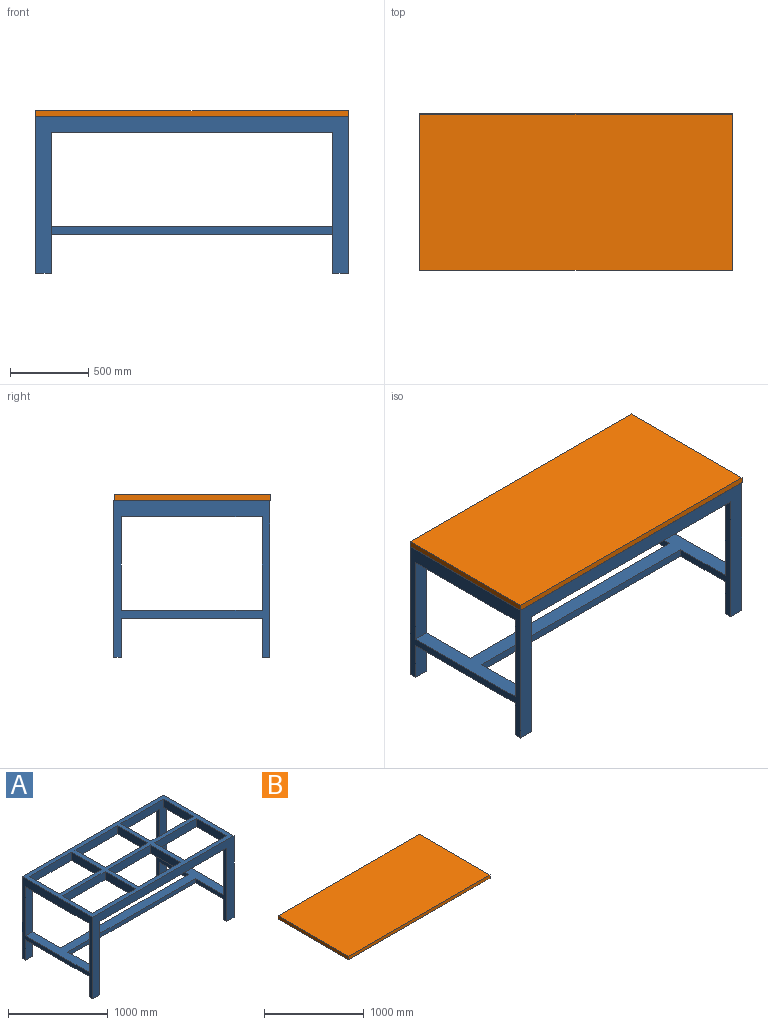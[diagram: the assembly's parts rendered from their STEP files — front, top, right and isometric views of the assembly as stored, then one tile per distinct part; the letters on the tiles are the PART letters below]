
ASSEMBLY  parts=2 mates=1
PART A: 46 faces, bbox 2000x1000x1000 mm
  f0: plane 900x450mm, normal (-1,0,0), area 65000mm2, adj f3,f6,f11,f31,f37,f42,f43,f44
  f1: plane 900x450mm, normal (1,0,0), area 65000mm2, adj f4,f6,f11,f15,f40,f42,f43,f44
  f2: plane 700x650mm, normal (0,1,0), area 120000mm2, adj f6,f7,f10,f16,f18,f36,f43
  f3: plane 700x650mm, normal (0,-1,0), area 120000mm2, adj f0,f6,f7,f10,f28,f30,f43
  f4: plane 700x650mm, normal (0,-1,0), area 120000mm2, adj f1,f6,f7,f8,f12,f14,f43
  f5: plane 700x650mm, normal (0,1,0), area 120000mm2, adj f6,f7,f8,f20,f22,f38,f43
  f6: plane 2000x1000mm, normal (0,0,-1), area 450000mm2, adj f0,f1,f2,f3,f4,f5,f8,f9
  f7: plane 2000x1000mm, normal (0,0,1), area 470000mm2, adj f2,f3,f4,f5,f8,f9,f10,f11
  f8: plane 1000x1000mm, normal (-1,0,0), area 235000mm2, adj f4,f5,f6,f7,f9,f11,f15,f21
  f9: plane 2000x1000mm, normal (0,-1,0), area 380000mm2, adj f6,f7,f8,f10,f36,f38,f39,f41
  f10: plane 1000x1000mm, normal (1,0,0), area 235000mm2, adj f2,f3,f6,f7,f9,f11,f17,f31
  f11: plane 2000x1000mm, normal (0,1,0), area 380000mm2, adj f0,f1,f6,f7,f8,f10,f37,f40
  f12: plane 425x100mm, normal (1,0,0), area 42500mm2, adj f4,f6,f7,f13
  f13: plane 600x100mm, normal (0,1,0), area 60000mm2, adj f6,f7,f12,f14
  f14: plane 425x100mm, normal (-1,0,0), area 42500mm2, adj f4,f6,f7,f13
  f15: plane 250x100mm, normal (0,-1,0), area 25000mm2, adj f1,f8,f40,f42
  f16: plane 425x100mm, normal (1,0,0), area 42500mm2, adj f2,f6,f7,f19
  f17: plane 250x100mm, normal (0,1,0), area 25000mm2, adj f10,f36,f41,f42
  f18: plane 425x100mm, normal (-1,0,0), area 42500mm2, adj f2,f6,f7,f19
  f19: plane 600x100mm, normal (0,-1,0), area 60000mm2, adj f6,f7,f16,f18
  f20: plane 425x100mm, normal (1,0,0), area 42500mm2, adj f5,f6,f7,f23
  f21: plane 250x100mm, normal (0,1,0), area 25000mm2, adj f8,f38,f39,f42
  f22: plane 425x100mm, normal (-1,0,0), area 42500mm2, adj f5,f6,f7,f23
  f23: plane 600x100mm, normal (0,-1,0), area 60000mm2, adj f6,f7,f20,f22
  f24: plane 425x100mm, normal (1,0,0), area 42500mm2, adj f6,f7,f25,f27
  f25: plane 600x100mm, normal (0,1,0), area 60000mm2, adj f6,f7,f24,f26
  f26: plane 425x100mm, normal (-1,0,0), area 42500mm2, adj f6,f7,f25,f27
  f27: plane 600x100mm, normal (0,-1,0), area 60000mm2, adj f6,f7,f24,f26
  f28: plane 425x100mm, normal (1,0,0), area 42500mm2, adj f3,f6,f7,f29
  f29: plane 600x100mm, normal (0,1,0), area 60000mm2, adj f6,f7,f28,f30
  f30: plane 425x100mm, normal (-1,0,0), area 42500mm2, adj f3,f6,f7,f29
  f31: plane 250x100mm, normal (0,-1,0), area 25000mm2, adj f0,f10,f37,f42
  f32: plane 425x100mm, normal (-1,0,0), area 42500mm2, adj f6,f7,f33,f35
  f33: plane 600x100mm, normal (0,-1,0), area 60000mm2, adj f6,f7,f32,f34
  f34: plane 425x100mm, normal (1,0,0), area 42500mm2, adj f6,f7,f33,f35
  f35: plane 600x100mm, normal (0,1,0), area 60000mm2, adj f6,f7,f32,f34
  f36: plane 900x450mm, normal (-1,0,0), area 65000mm2, adj f2,f6,f9,f17,f41,f42,f43,f45
  f37: plane 100x50mm, normal (0,0,-1), area 5000mm2, adj f0,f10,f11,f31
  f38: plane 900x450mm, normal (1,0,0), area 65000mm2, adj f5,f6,f9,f21,f39,f42,f43,f45
  f39: plane 100x50mm, normal (0,0,-1), area 5000mm2, adj f8,f9,f21,f38
  f40: plane 100x50mm, normal (0,0,-1), area 5000mm2, adj f1,f8,f11,f15
  f41: plane 100x50mm, normal (0,0,-1), area 5000mm2, adj f9,f10,f17,f36
  f42: plane 2000x900mm, normal (0,0,-1), area 360000mm2, adj f0,f1,f8,f10,f15,f17,f21,f31
  f43: plane 2000x900mm, normal (0,0,1), area 360000mm2, adj f0,f1,f2,f3,f4,f5,f8,f10
  f44: plane 1800x50mm, normal (0,1,0), area 90000mm2, adj f0,f1,f42,f43
  f45: plane 1800x50mm, normal (0,-1,0), area 90000mm2, adj f36,f38,f42,f43
PART B: 6 faces, bbox 2000x1000x40 mm
  f0: plane 2000x40mm, normal (0,1,0), area 80000mm2, adj f1,f3,f4,f5
  f1: plane 1000x40mm, normal (-1,0,0), area 40000mm2, adj f0,f2,f4,f5
  f2: plane 2000x40mm, normal (0,-1,0), area 80000mm2, adj f1,f3,f4,f5
  f3: plane 1000x40mm, normal (1,0,0), area 40000mm2, adj f0,f2,f4,f5
  f4: plane 2000x1000mm, normal (0,0,1), area 2000000mm2, adj f0,f1,f2,f3
  f5: plane 2000x1000mm, normal (0,0,-1), area 2000000mm2, adj f0,f1,f2,f3
PLACE A t=(-32.39,226.52,975.71)mm
PLACE B t=(-31.51,375.92,1075.71)mm
MATE parallel A.f7 <-> B.f5  axis (0,0,1) through (-21.79,354.1,1075.71)mm
